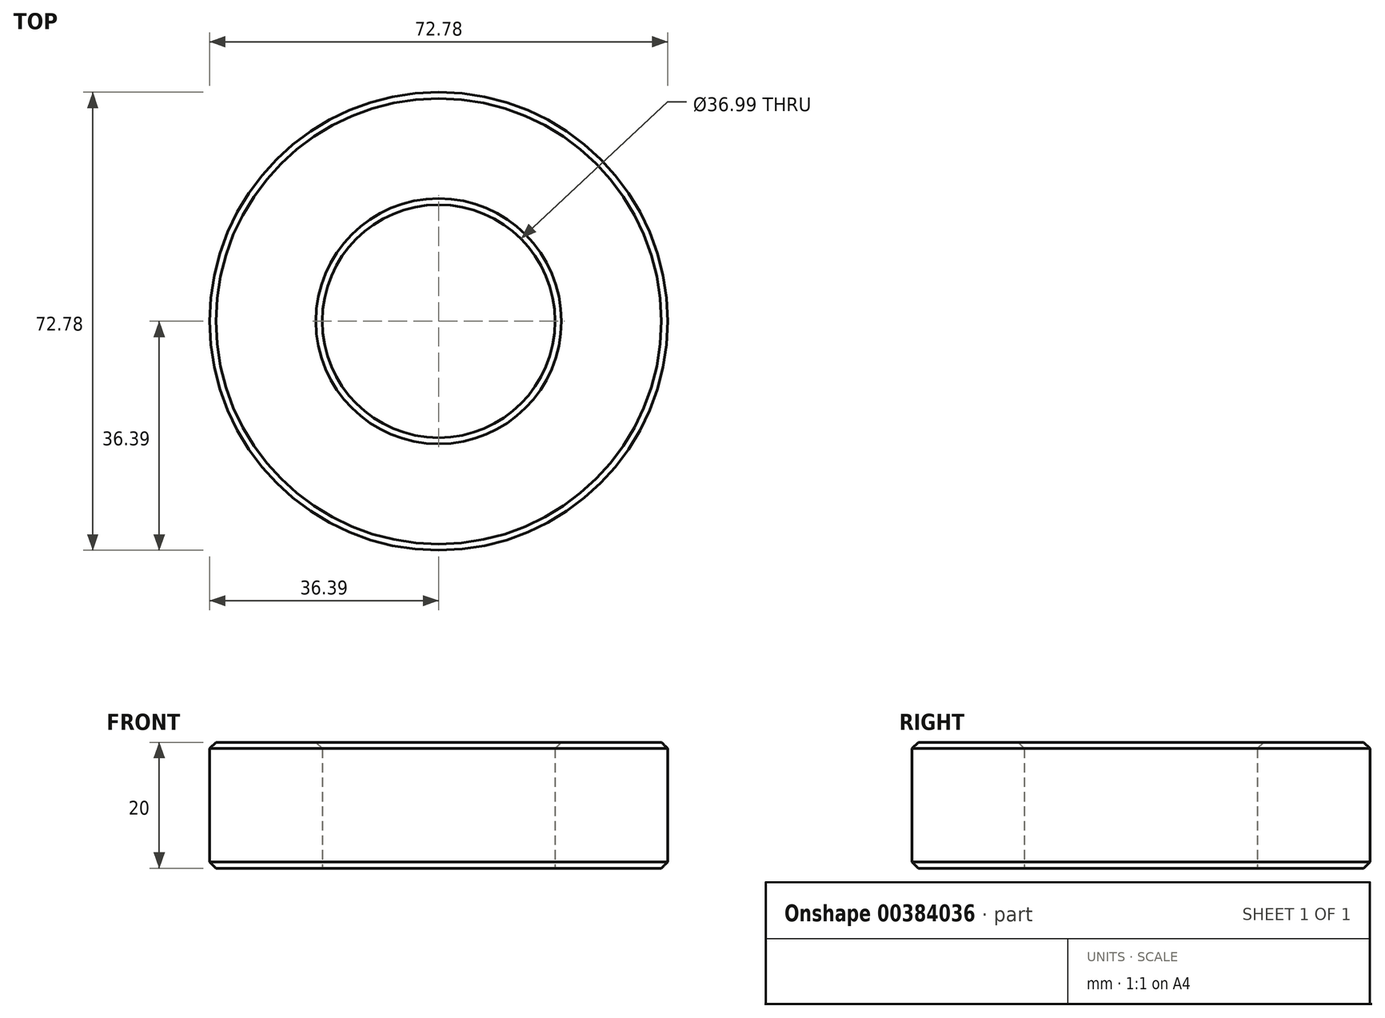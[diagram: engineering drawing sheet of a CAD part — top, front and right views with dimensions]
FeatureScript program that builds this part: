
annotation { "Feature Type Name" : "Feature", "Feature Type Description" : "" }
export const myFeature = defineFeature(function(context is Context, id is Id, definition is map)
    precondition{}
    {
        {
            var Q0;
            Q0=qCreatedBy(makeId("Top.planeOp"),FACE);
            var sketch = newSketch(context, id + "F0", { "sketchPlane" : qUnion([Q0])});
            skCircle(sketch, "E0", {"center": v(0, 0) * mm, "radius": 36.39 * mm});
            skCircle(sketch, "E1", {"center": v(0, 0) * mm, "radius": 18.5 * mm});
            skSolve(sketch);
        }
        {
            var Q0;
            Q0 = qSketchRegion(id + "F0", true);
            var sketch = newSketch(context, id + "F1", { "sketchPlane" : qUnion([Q0])});
            skSolve(sketch);
        }
        {
            var Q0;
            Q0=makeQuery(id+"F1.imprint","IMPRINT",FACE,{"disambiguationData":[TD([[makeQuery(id+"F1.imprint","IMPRINT",EDGE,{"derivedFrom":makeQuery(id+"F0.imprint","IMPRINT",EDGE,{"derivedFrom":sQuery(id+"F0.wireOp",EDGE,"E0")})}),1.0]])]});
            extrude(context, id + "F2", {"entities" : qUnion([Q0]), "depth" : 20 * mm});
        }
        {
            var Q0;
            Q0=makeQuery(id+"F2.opExtrude","CAP_EDGE",EDGE,{"disambiguationData":[OSD([sQuery(id+"F0.wireOp",EDGE,"E0")])],"isStart":false});
            var Q1;
            Q1=makeQuery(id+"F2.opExtrude","CAP_EDGE",EDGE,{"disambiguationData":[OSD([sQuery(id+"F0.wireOp",EDGE,"E0")])],"isStart":true});
            chamfer(context, id + "F3", {"entities" : qUnion([Q0, Q1]), "width" : 1 * mm, "tangentPropagation" : true});
        }
        {
            var Q0;
            Q0=makeQuery(id+"F2.opExtrude","CAP_EDGE",EDGE,{"disambiguationData":[OSD([sQuery(id+"F0.wireOp",EDGE,"E1")])],"isStart":false});
            chamfer(context, id + "F4", {"entities" : qUnion([Q0]), "width" : 1 * mm, "tangentPropagation" : true});
        }
    });
